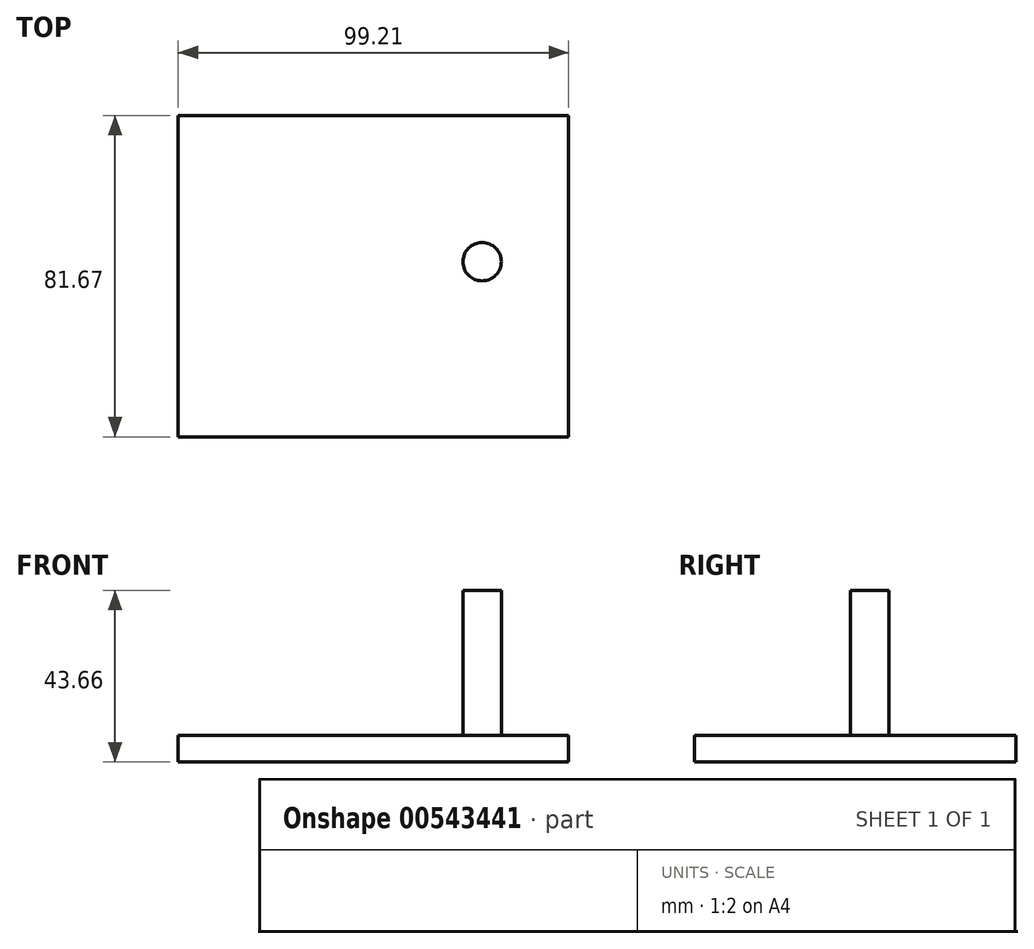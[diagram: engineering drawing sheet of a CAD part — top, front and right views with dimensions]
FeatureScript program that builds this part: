
annotation { "Feature Type Name" : "Feature", "Feature Type Description" : "" }
export const myFeature = defineFeature(function(context is Context, id is Id, definition is map)
    precondition{}
    {
        {
            var Q0;
            Q0=qCreatedBy(makeId("Top.planeOp"),FACE);
            var sketch = newSketch(context, id + "F0", { "sketchPlane" : qUnion([Q0])});
            skLineSegment(sketch, "E0.bottom", {"start": v(-65.42, 44.66) * mm, "end": v(33.8, 44.66) * mm});
            skLineSegment(sketch, "E0.top", {"start": v(-65.42, -37.01) * mm, "end": v(33.8, -37.01) * mm});
            skLineSegment(sketch, "E0.left", {"start": v(-65.42, 44.66) * mm, "end": v(-65.42, -37.01) * mm});
            skLineSegment(sketch, "E0.right", {"start": v(33.8, 44.66) * mm, "end": v(33.8, -37.01) * mm});
            skSolve(sketch);
        }
        {
            var Q0;
            Q0=makeQuery(id+"F0.imprint","IMPRINT",FACE,{"disambiguationData":[TD([[makeQuery(id+"F0.imprint","IMPRINT",EDGE,{"derivedFrom":sQuery(id+"F0.wireOp",EDGE,"E0.bottom")}),-1.0]])]});
            var sketch = newSketch(context, id + "F1", { "sketchPlane" : qUnion([Q0])});
            skSolve(sketch);
        }
        {
            var Q0;
            Q0=makeQuery(id+"F1.imprint","IMPRINT",FACE,{"disambiguationData":[TD([[makeQuery(id+"F1.imprint","IMPRINT",EDGE,{"derivedFrom":makeQuery(id+"F0.imprint","IMPRINT",EDGE,{"derivedFrom":sQuery(id+"F0.wireOp",EDGE,"E0.bottom")})}),-1.0]])]});
            extrude(context, id + "F2", {"entities" : qUnion([Q0]), "depth" : 6.8 * mm, "offsetDistance" : 25.4 * mm});
        }
        {
            var Q0;
            Q0=makeQuery(id+"F2.opExtrude","CAP_FACE",FACE,{"disambiguationData":[OSD([sQuery(id+"F0.wireOp",EDGE,"E0.bottom"),sQuery(id+"F0.wireOp",EDGE,"E0.top"),sQuery(id+"F0.wireOp",EDGE,"E0.left"),sQuery(id+"F0.wireOp",EDGE,"E0.right")])],"isStart":false});
            var sketch = newSketch(context, id + "F3", { "sketchPlane" : qUnion([Q0])});
            skCircle(sketch, "E1", {"center": v(11.8, 7.48) * mm, "radius": 4.87 * mm});
            skSolve(sketch);
        }
        {
            var Q0;
            Q0 = qSketchRegion(id + "F3", true);
            extrude(context, id + "F4", {"entities" : qUnion([Q0]), "operationType" : NewBodyOperationType.ADD, "depth" : 36.86 * mm, "offsetDistance" : 25.4 * mm});
        }
    });
